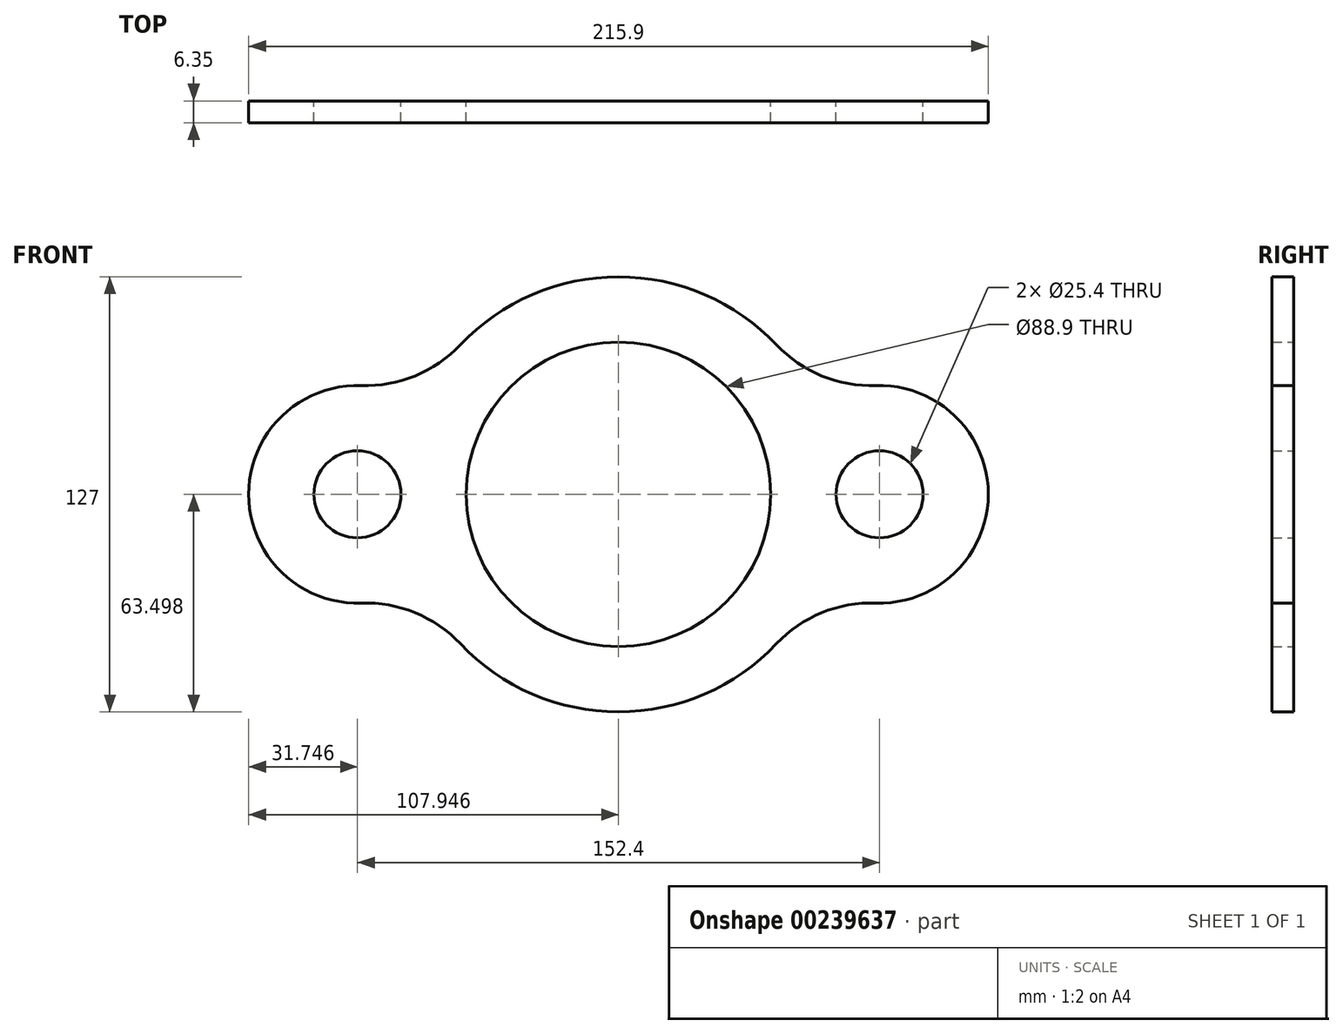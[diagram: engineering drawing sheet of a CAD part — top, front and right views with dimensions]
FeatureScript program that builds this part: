
annotation { "Feature Type Name" : "Feature", "Feature Type Description" : "" }
export const myFeature = defineFeature(function(context is Context, id is Id, definition is map)
    precondition{}
    {
        {
            var Q0;
            Q0=qCreatedBy(makeId("Front.planeOp"),FACE);
            var sketch = newSketch(context, id + "F0", { "sketchPlane" : qUnion([Q0])});
            skCircle(sketch, "E0", {"center": v(-32.6, 22.74) * mm, "radius": 44.45 * mm});
            skArc(sketch, "E1", {"start": v(-78.74, -20.9) * mm, "mid": v(-32.6, -40.76) * mm, "end": v(13.53, -20.9) * mm});
            skPoint(sketch, "E2.center.orphan", {"position": v(-135.82, 22.74) * mm});
            skArc(sketch, "E3", {"start": v(-107.72, 54.47) * mm, "mid": v(-140.55, 22.74) * mm, "end": v(-107.72, -9) * mm});
            skCircle(sketch, "E4", {"center": v(-108.8, 22.74) * mm, "radius": 12.7 * mm});
            skArc(sketch, "E5", {"start": v(42.51, -9) * mm, "mid": v(75.35, 22.74) * mm, "end": v(42.51, 54.47) * mm});
            skCircle(sketch, "E6", {"center": v(43.6, 22.74) * mm, "radius": 12.7 * mm});
            skLineSegment(sketch, "E7", {"start": v(-32.6, 22.74) * mm, "end": v(-108.8, 22.74) * mm, "construction": true});
            skLineSegment(sketch, "E8", {"start": v(-32.6, 22.74) * mm, "end": v(43.6, 22.74) * mm, "construction": true});
            skArc(sketch, "E9.trimOffspring", {"start": v(13.53, 66.37) * mm, "mid": v(-32.6, 86.24) * mm, "end": v(-78.74, 66.37) * mm});
            skPoint(sketch, "E10.visualSharp", {"position": v(-90.55, 48.71) * mm});
            skArc(sketch, "E10.filletArc", {"start": v(-107.72, 54.47) * mm, "mid": v(-91.95, 57.3) * mm, "end": v(-78.74, 66.37) * mm});
            skPoint(sketch, "E11.visualSharp", {"position": v(25.34, 48.71) * mm});
            skArc(sketch, "E11.filletArc", {"start": v(13.53, 66.37) * mm, "mid": v(26.74, 57.3) * mm, "end": v(42.51, 54.47) * mm});
            skPoint(sketch, "E12.visualSharp", {"position": v(25.34, -3.24) * mm});
            skArc(sketch, "E12.filletArc", {"start": v(42.51, -9) * mm, "mid": v(26.74, -11.83) * mm, "end": v(13.53, -20.9) * mm});
            skPoint(sketch, "E13.visualSharp", {"position": v(-90.55, -3.24) * mm});
            skArc(sketch, "E13.filletArc", {"start": v(-78.74, -20.9) * mm, "mid": v(-91.95, -11.83) * mm, "end": v(-107.72, -9) * mm});
            skSolve(sketch);
        }
        {
            var Q0;
            Q0 = qSketchRegion(id + "F0", true);
            extrude(context, id + "F1", {"entities" : qUnion([Q0]), "depth" : 6.35 * mm});
        }
    });
